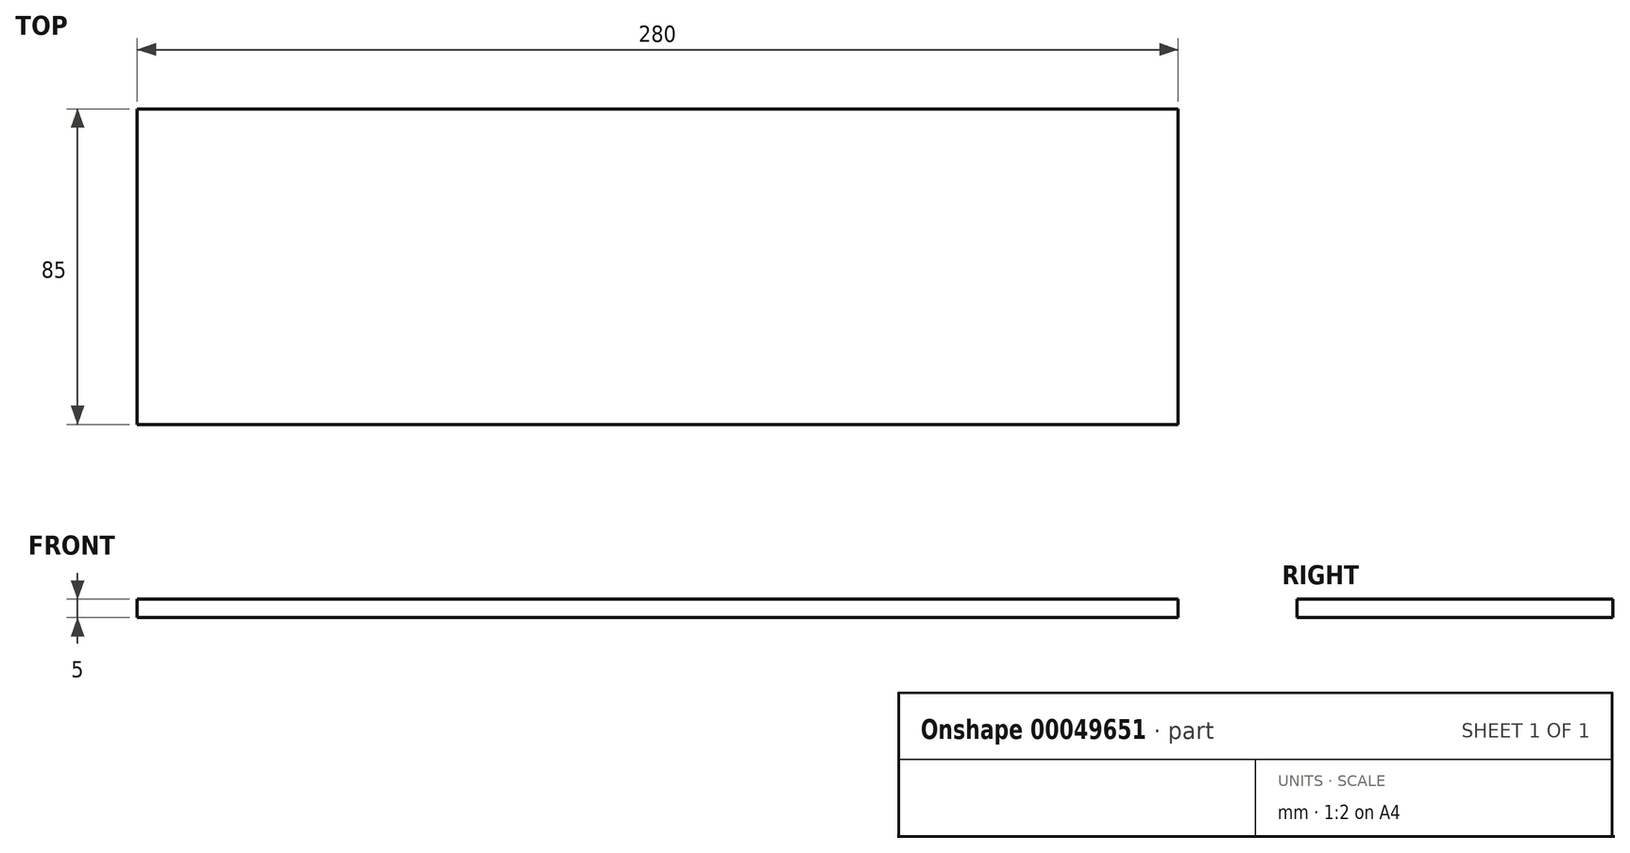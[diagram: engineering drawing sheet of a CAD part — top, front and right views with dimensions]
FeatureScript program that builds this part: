
annotation { "Feature Type Name" : "Feature", "Feature Type Description" : "" }
export const myFeature = defineFeature(function(context is Context, id is Id, definition is map)
    precondition{}
    {
        {
            var Q0;
            Q0=qCreatedBy(makeId("Top.planeOp"),FACE);
            var sketch = newSketch(context, id + "F0", { "sketchPlane" : qUnion([Q0])});
            skLineSegment(sketch, "E0.bottom", {"start": v(0, 0) * mm, "end": v(280, 0) * mm});
            skLineSegment(sketch, "E0.top", {"start": v(0, 85) * mm, "end": v(280, 85) * mm});
            skLineSegment(sketch, "E0.left", {"start": v(0, 0) * mm, "end": v(0, 85) * mm});
            skLineSegment(sketch, "E0.right", {"start": v(280, 0) * mm, "end": v(280, 85) * mm});
            skSolve(sketch);
        }
        {
            var Q0;
            Q0=makeQuery(id+"F0.imprint","IMPRINT",FACE,{"disambiguationData":[TD([[makeQuery(id+"F0.imprint","IMPRINT",EDGE,{"derivedFrom":sQuery(id+"F0.wireOp",EDGE,"E0.bottom")}),1.0]])]});
            extrude(context, id + "F1", {"entities" : qUnion([Q0]), "depth" : 5 * mm});
        }
    });
